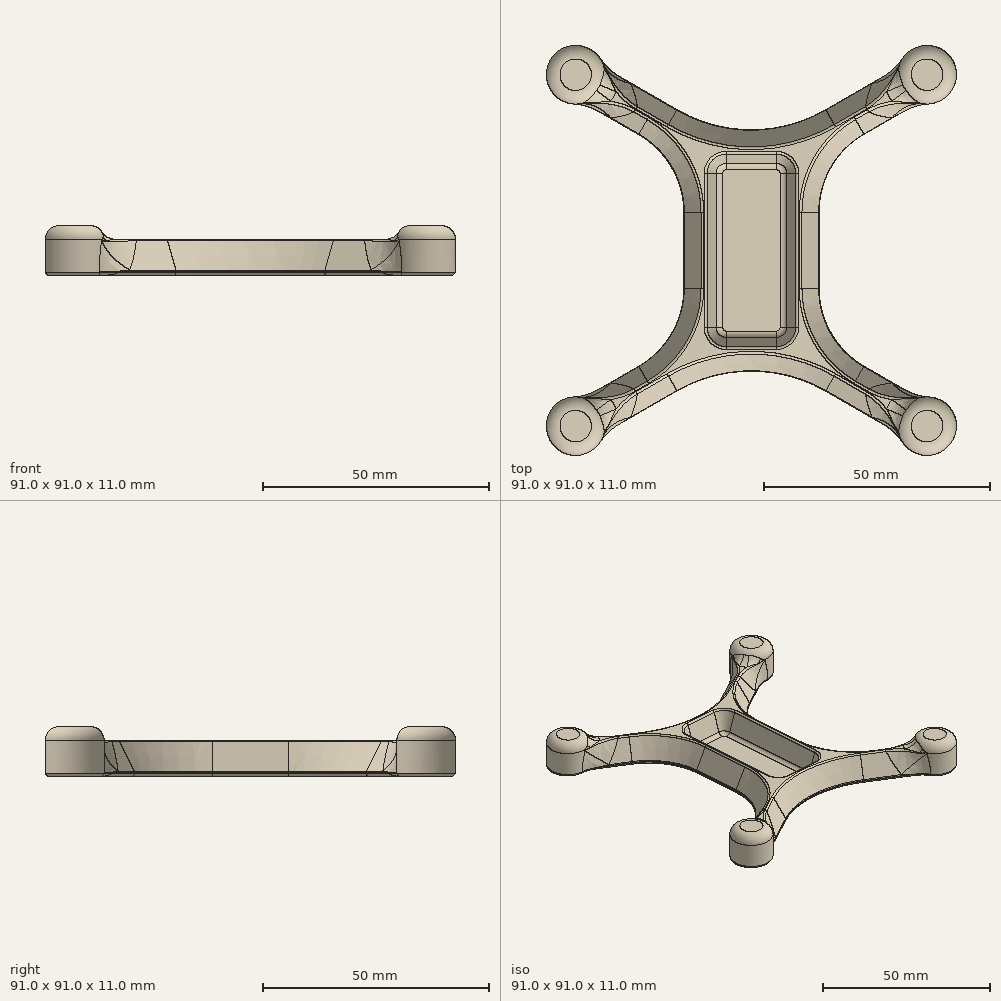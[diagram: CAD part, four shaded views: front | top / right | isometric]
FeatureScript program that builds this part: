
annotation { "Feature Type Name" : "Feature", "Feature Type Description" : "" }
export const myFeature = defineFeature(function(context is Context, id is Id, definition is map)
    precondition{}
    {
        {
            var Q0;
            Q0=qCreatedBy(makeId("Top.planeOp"),FACE);
            var sketch = newSketch(context, id + "F0", { "sketchPlane" : qUnion([Q0])});
            skLineSegment(sketch, "E0", {"start": v(-32.69, 40.55) * mm, "end": v(0, 21.68) * mm});
            skLineSegment(sketch, "E1", {"start": v(0, 21.68) * mm, "end": v(32.69, 40.55) * mm});
            skLineSegment(sketch, "E2", {"start": v(-32.69, -40.55) * mm, "end": v(0, -21.68) * mm});
            skLineSegment(sketch, "E3", {"start": v(0, -21.68) * mm, "end": v(32.69, -40.55) * mm});
            skLineSegment(sketch, "E4", {"start": v(-37.19, 32.76) * mm, "end": v(-15, 19.95) * mm});
            skLineSegment(sketch, "E5", {"start": v(-15, 19.95) * mm, "end": v(-15, -19.95) * mm});
            skLineSegment(sketch, "E6", {"start": v(-15, -19.95) * mm, "end": v(-37.19, -32.76) * mm});
            skLineSegment(sketch, "E7", {"start": v(37.19, -32.76) * mm, "end": v(15, -19.95) * mm});
            skLineSegment(sketch, "E8", {"start": v(15, -19.95) * mm, "end": v(15, 19.95) * mm});
            skLineSegment(sketch, "E9", {"start": v(15, 19.95) * mm, "end": v(37.19, 32.76) * mm});
            skArc(sketch, "E10", {"start": v(-37.19, 32.76) * mm, "mid": v(-44.63, 42.25) * mm, "end": v(-32.69, 40.55) * mm});
            skArc(sketch, "E11", {"start": v(37.19, 32.76) * mm, "mid": v(44.63, 42.25) * mm, "end": v(32.69, 40.55) * mm});
            skArc(sketch, "E12", {"start": v(37.19, -32.76) * mm, "mid": v(44.63, -42.25) * mm, "end": v(32.69, -40.55) * mm});
            skArc(sketch, "E13", {"start": v(-37.19, -32.76) * mm, "mid": v(-44.63, -42.25) * mm, "end": v(-32.69, -40.55) * mm});
            skArc(sketch, "E14", {"start": v(-34.08, 38.37) * mm, "mid": v(-33.8, 36) * mm, "end": v(-36, 35.05) * mm});
            skArc(sketch, "E15", {"start": v(34.08, 38.37) * mm, "mid": v(33.8, 36) * mm, "end": v(36, 35.05) * mm});
            skArc(sketch, "E16", {"start": v(-36, -35.05) * mm, "mid": v(-33.8, -36) * mm, "end": v(-34.08, -38.37) * mm});
            skArc(sketch, "E17", {"start": v(36, -35.05) * mm, "mid": v(33.8, -36) * mm, "end": v(34.08, -38.37) * mm});
            skArc(sketch, "E18", {"start": v(37.64, -34.97) * mm, "mid": v(42.68, -41.12) * mm, "end": v(34.83, -39.83) * mm});
            skArc(sketch, "E19", {"start": v(-37.64, -34.97) * mm, "mid": v(-42.68, -41.12) * mm, "end": v(-34.83, -39.83) * mm});
            skArc(sketch, "E20", {"start": v(-34.83, 39.83) * mm, "mid": v(-42.68, 41.13) * mm, "end": v(-37.64, 34.97) * mm});
            skArc(sketch, "E21", {"start": v(37.64, 34.97) * mm, "mid": v(42.68, 41.13) * mm, "end": v(34.83, 39.83) * mm});
            skPoint(sketch, "E22.visualSharp", {"position": v(-34.75, 38.84) * mm});
            skArc(sketch, "E22.filletArc", {"start": v(-34.83, 39.83) * mm, "mid": v(-34.56, 39.05) * mm, "end": v(-34.08, 38.37) * mm});
            skPoint(sketch, "E23.visualSharp", {"position": v(-36.74, 35.4) * mm});
            skArc(sketch, "E23.filletArc", {"start": v(-36, 35.05) * mm, "mid": v(-36.82, 35.13) * mm, "end": v(-37.64, 34.97) * mm});
            skPoint(sketch, "E24.visualSharp", {"position": v(34.75, 38.84) * mm});
            skArc(sketch, "E24.filletArc", {"start": v(34.08, 38.37) * mm, "mid": v(34.56, 39.05) * mm, "end": v(34.83, 39.83) * mm});
            skPoint(sketch, "E25.visualSharp", {"position": v(36.74, 35.4) * mm});
            skArc(sketch, "E25.filletArc", {"start": v(37.64, 34.97) * mm, "mid": v(36.82, 35.13) * mm, "end": v(36, 35.05) * mm});
            skPoint(sketch, "E26.visualSharp", {"position": v(36.74, -35.4) * mm});
            skArc(sketch, "E26.filletArc", {"start": v(36, -35.05) * mm, "mid": v(36.82, -35.13) * mm, "end": v(37.64, -34.97) * mm});
            skPoint(sketch, "E27.visualSharp", {"position": v(34.75, -38.84) * mm});
            skArc(sketch, "E27.filletArc", {"start": v(34.83, -39.83) * mm, "mid": v(34.56, -39.05) * mm, "end": v(34.08, -38.37) * mm});
            skPoint(sketch, "E28.visualSharp", {"position": v(-36.74, -35.4) * mm});
            skArc(sketch, "E28.filletArc", {"start": v(-37.64, -34.97) * mm, "mid": v(-36.82, -35.13) * mm, "end": v(-36, -35.05) * mm});
            skPoint(sketch, "E29.visualSharp", {"position": v(-34.75, -38.84) * mm});
            skArc(sketch, "E29.filletArc", {"start": v(-34.08, -38.37) * mm, "mid": v(-34.56, -39.05) * mm, "end": v(-34.83, -39.83) * mm});
            skSolve(sketch);
        }
        {
            var Q0;
            Q0 = qSketchRegion(id + "F0", true);
            extrude(context, id + "F1", {"entities" : qUnion([Q0]), "depth" : 8 * mm, "offsetDistance" : 25 * mm});
        }
        {
            var Q0;
            Q0=qCreatedBy(makeId("Front.planeOp"),FACE);
            var sketch = newSketch(context, id + "F2", { "sketchPlane" : qUnion([Q0])});
            skLineSegment(sketch, "E30.bottom", {"start": v(-7.5, 10.6) * mm, "end": v(7.5, 10.6) * mm});
            skLineSegment(sketch, "E30.top", {"start": v(-7.5, 0.6) * mm, "end": v(7.5, 0.6) * mm});
            skLineSegment(sketch, "E30.left", {"start": v(-7.5, 10.6) * mm, "end": v(-7.5, 0.6) * mm});
            skLineSegment(sketch, "E30.right", {"start": v(7.5, 10.6) * mm, "end": v(7.5, 0.6) * mm});
            skSolve(sketch);
        }
        {
            var Q0;
            Q0 = qSketchRegion(id + "F2", true);
            extrude(context, id + "F3", {"entities" : qUnion([Q0]), "operationType" : NewBodyOperationType.REMOVE, "oppositeDirection" : true, "depth" : 19 * mm, "offsetDistance" : 25 * mm, "hasSecondDirection" : true, "secondDirectionOppositeDirection" : false, "secondDirectionDepth" : 19 * mm});
        }
        {
            var Q0;
            Q0=makeQuery(id+"F1.opExtrude","CAP_FACE",FACE,{"disambiguationData":[OSD([sQuery(id+"F0.wireOp",EDGE,"E0"),sQuery(id+"F0.wireOp",EDGE,"E1"),sQuery(id+"F0.wireOp",EDGE,"E2"),sQuery(id+"F0.wireOp",EDGE,"E3"),sQuery(id+"F0.wireOp",EDGE,"E4"),sQuery(id+"F0.wireOp",EDGE,"E5"),sQuery(id+"F0.wireOp",EDGE,"E6"),sQuery(id+"F0.wireOp",EDGE,"E7"),sQuery(id+"F0.wireOp",EDGE,"E8"),sQuery(id+"F0.wireOp",EDGE,"E9"),sQuery(id+"F0.wireOp",EDGE,"E10"),sQuery(id+"F0.wireOp",EDGE,"E11"),sQuery(id+"F0.wireOp",EDGE,"E12"),sQuery(id+"F0.wireOp",EDGE,"E13"),sQuery(id+"F0.wireOp",EDGE,"E14"),sQuery(id+"F0.wireOp",EDGE,"E15"),sQuery(id+"F0.wireOp",EDGE,"E16"),sQuery(id+"F0.wireOp",EDGE,"E17"),sQuery(id+"F0.wireOp",EDGE,"E18"),sQuery(id+"F0.wireOp",EDGE,"E19"),sQuery(id+"F0.wireOp",EDGE,"E20"),sQuery(id+"F0.wireOp",EDGE,"E21")])],"isStart":false});
            var sketch = newSketch(context, id + "F4", { "sketchPlane" : qUnion([Q0])});
            skCircle(sketch, "E31", {"center": v(-39, 39) * mm, "radius": 6.5 * mm});
            skCircle(sketch, "E32", {"center": v(39, 39) * mm, "radius": 6.5 * mm});
            skCircle(sketch, "E33", {"center": v(39, -39) * mm, "radius": 6.5 * mm});
            skCircle(sketch, "E34", {"center": v(-39, -39) * mm, "radius": 6.5 * mm});
            skSolve(sketch);
        }
        {
            var Q0;
            Q0 = qSketchRegion(id + "F4", true);
            extrude(context, id + "F5", {"entities" : qUnion([Q0]), "operationType" : NewBodyOperationType.ADD, "depth" : 3 * mm, "offsetDistance" : 25 * mm});
        }
        {
            var Q0;
            Q0=makeQuery(id+"F1.opExtrude","SWEPT_EDGE",EDGE,{"disambiguationData":[OSD([sQuery(id+"F0.wireOp",EDGE,"E0"),sQuery(id+"F0.wireOp",EDGE,"E1")])]});
            var Q1;
            Q1=makeQuery(id+"F1.opExtrude","SWEPT_EDGE",EDGE,{"disambiguationData":[OSD([sQuery(id+"F0.wireOp",EDGE,"E2"),sQuery(id+"F0.wireOp",EDGE,"E3")])]});
            fillet(context, id + "F6", {"entities" : qUnion([Q0, Q1]), "radius" : 33 * mm, "tangentPropagation" : true, "allowEdgeOverflow" : false});
        }
        {
            var Q0;
            Q0=makeQuery(id+"F1.opExtrude","SWEPT_EDGE",EDGE,{"disambiguationData":[OSD([sQuery(id+"F0.wireOp",EDGE,"E4"),sQuery(id+"F0.wireOp",EDGE,"E5")])]});
            var Q1;
            Q1=makeQuery(id+"F1.opExtrude","SWEPT_EDGE",EDGE,{"disambiguationData":[OSD([sQuery(id+"F0.wireOp",EDGE,"E5"),sQuery(id+"F0.wireOp",EDGE,"E6")])]});
            var Q2;
            Q2=makeQuery(id+"F1.opExtrude","SWEPT_EDGE",EDGE,{"disambiguationData":[OSD([sQuery(id+"F0.wireOp",EDGE,"E8"),sQuery(id+"F0.wireOp",EDGE,"E9")])]});
            var Q3;
            Q3=makeQuery(id+"F1.opExtrude","SWEPT_EDGE",EDGE,{"disambiguationData":[OSD([sQuery(id+"F0.wireOp",EDGE,"E7"),sQuery(id+"F0.wireOp",EDGE,"E8")])]});
            fillet(context, id + "F7", {"entities" : qUnion([Q0, Q1, Q2, Q3]), "radius" : 20 * mm, "tangentPropagation" : true, "allowEdgeOverflow" : false});
        }
        {
            var Q0;
            Q0=makeQuery(id+"F1.opExtrude","CAP_EDGE",EDGE,{"disambiguationData":[OSD([sQuery(id+"F0.wireOp",EDGE,"E2")])],"isStart":false});
            var Q1;
            Q1=makeQuery(id+"F1.opExtrude","CAP_EDGE",EDGE,{"disambiguationData":[OSD([sQuery(id+"F0.wireOp",EDGE,"E6")])],"isStart":false});
            var Q2;
            Q2=makeQuery(id+"F1.opExtrude","CAP_EDGE",EDGE,{"disambiguationData":[OSD([sQuery(id+"F0.wireOp",EDGE,"E3")])],"isStart":false});
            var Q3;
            Q3=makeQuery(id+"F1.opExtrude","CAP_EDGE",EDGE,{"disambiguationData":[OSD([sQuery(id+"F0.wireOp",EDGE,"E7")])],"isStart":false});
            var Q4;
            Q4=makeQuery(id+"F1.opExtrude","CAP_EDGE",EDGE,{"disambiguationData":[OSD([sQuery(id+"F0.wireOp",EDGE,"E1")])],"isStart":false});
            var Q5;
            Q5=makeQuery(id+"F1.opExtrude","CAP_EDGE",EDGE,{"disambiguationData":[OSD([sQuery(id+"F0.wireOp",EDGE,"E0")])],"isStart":false});
            var Q6;
            Q6=makeQuery(id+"F1.opExtrude","CAP_EDGE",EDGE,{"disambiguationData":[OSD([sQuery(id+"F0.wireOp",EDGE,"E4")])],"isStart":false});
            var Q7;
            Q7=makeQuery(id+"F1.opExtrude","CAP_EDGE",EDGE,{"disambiguationData":[OSD([sQuery(id+"F0.wireOp",EDGE,"E9")])],"isStart":false});
            chamfer(context, id + "F8", {"entities" : qUnion([Q0, Q1, Q2, Q3, Q4, Q5, Q6, Q7]), "chamferType" : ChamferType.TWO_OFFSETS, "width1" : 4 * mm, "oppositeDirection" : false, "width2" : 7 * mm, "tangentPropagation" : true});
        }
        {
            var Q0;
            Q0=makeQuery(id+"F3.boolean.opBoolean","COPY",EDGE,{"derivedFrom":makeQuery(id+"F3.opExtrude","CAP_EDGE",EDGE,{"disambiguationData":[OSD([sQuery(id+"F2.wireOp",EDGE,"E30.left")])],"isStart":false})});
            var Q1;
            Q1=makeQuery(id+"F3.boolean.opBoolean","COPY",EDGE,{"derivedFrom":makeQuery(id+"F3.opExtrude","CAP_EDGE",EDGE,{"disambiguationData":[OSD([sQuery(id+"F2.wireOp",EDGE,"E30.right")])],"isStart":false})});
            var Q2;
            Q2=makeQuery(id+"F3.boolean.opBoolean","COPY",EDGE,{"derivedFrom":makeQuery(id+"F3.opExtrude","CAP_EDGE",EDGE,{"disambiguationData":[OSD([sQuery(id+"F2.wireOp",EDGE,"E30.left")])],"isStart":true})});
            var Q3;
            Q3=makeQuery(id+"F3.boolean.opBoolean","COPY",EDGE,{"derivedFrom":makeQuery(id+"F3.opExtrude","CAP_EDGE",EDGE,{"disambiguationData":[OSD([sQuery(id+"F2.wireOp",EDGE,"E30.right")])],"isStart":true})});
            fillet(context, id + "F9", {"entities" : qUnion([Q0, Q1, Q2, Q3]), "radius" : 2 * mm, "tangentPropagation" : true, "allowEdgeOverflow" : false});
        }
        {
            var Q0;
            Q0=makeQuery(id+"F3.boolean.opBoolean","INTERSECT",EDGE,{"derivedFrom":[makeQuery(id+"F1.opExtrude","CAP_FACE",FACE,{"disambiguationData":[OSD([sQuery(id+"F0.wireOp",EDGE,"E0"),sQuery(id+"F0.wireOp",EDGE,"E1"),sQuery(id+"F0.wireOp",EDGE,"E2"),sQuery(id+"F0.wireOp",EDGE,"E3"),sQuery(id+"F0.wireOp",EDGE,"E4"),sQuery(id+"F0.wireOp",EDGE,"E5"),sQuery(id+"F0.wireOp",EDGE,"E6"),sQuery(id+"F0.wireOp",EDGE,"E7"),sQuery(id+"F0.wireOp",EDGE,"E8"),sQuery(id+"F0.wireOp",EDGE,"E9"),sQuery(id+"F0.wireOp",EDGE,"E10"),sQuery(id+"F0.wireOp",EDGE,"E11"),sQuery(id+"F0.wireOp",EDGE,"E12"),sQuery(id+"F0.wireOp",EDGE,"E13"),sQuery(id+"F0.wireOp",EDGE,"E14"),sQuery(id+"F0.wireOp",EDGE,"E15"),sQuery(id+"F0.wireOp",EDGE,"E16"),sQuery(id+"F0.wireOp",EDGE,"E17"),sQuery(id+"F0.wireOp",EDGE,"E18"),sQuery(id+"F0.wireOp",EDGE,"E19"),sQuery(id+"F0.wireOp",EDGE,"E20"),sQuery(id+"F0.wireOp",EDGE,"E21"),sQuery(id+"F0.wireOp",EDGE,"E22.filletArc"),sQuery(id+"F0.wireOp",EDGE,"E23.filletArc"),sQuery(id+"F0.wireOp",EDGE,"E24.filletArc"),sQuery(id+"F0.wireOp",EDGE,"E25.filletArc"),sQuery(id+"F0.wireOp",EDGE,"E26.filletArc"),sQuery(id+"F0.wireOp",EDGE,"E27.filletArc"),sQuery(id+"F0.wireOp",EDGE,"E28.filletArc"),sQuery(id+"F0.wireOp",EDGE,"E29.filletArc")])],"isStart":false}),makeQuery(id+"F3.opExtrude","CAP_FACE",FACE,{"disambiguationData":[OSD([sQuery(id+"F2.wireOp",EDGE,"E30.bottom"),sQuery(id+"F2.wireOp",EDGE,"E30.top"),sQuery(id+"F2.wireOp",EDGE,"E30.left"),sQuery(id+"F2.wireOp",EDGE,"E30.right")])],"isStart":false})]});
            chamfer(context, id + "F10", {"entities" : qUnion([Q0]), "chamferType" : ChamferType.TWO_OFFSETS, "width1" : 2.5 * mm, "oppositeDirection" : false, "width2" : 7.4 * mm, "tangentPropagation" : true});
        }
        {
            var Q0;
            Q0=makeQuery(id+"F5.opExtrude","CAP_FACE",FACE,{"disambiguationData":[OSD([sQuery(id+"F4.wireOp",EDGE,"E34")])],"isStart":true});
            var Q1;
            Q1=makeQuery(id+"F5.opExtrude","CAP_FACE",FACE,{"disambiguationData":[OSD([sQuery(id+"F4.wireOp",EDGE,"E33")])],"isStart":true});
            var Q2;
            Q2=makeQuery(id+"F5.opExtrude","CAP_FACE",FACE,{"disambiguationData":[OSD([sQuery(id+"F4.wireOp",EDGE,"E32")])],"isStart":true});
            var Q3;
            Q3=makeQuery(id+"F5.opExtrude","CAP_FACE",FACE,{"disambiguationData":[OSD([sQuery(id+"F4.wireOp",EDGE,"E31")])],"isStart":true});
            fillet(context, id + "F11", {"entities" : qUnion([Q0, Q1, Q2, Q3]), "radius" : 2 * mm, "tangentPropagation" : true, "allowEdgeOverflow" : false});
        }
        {
            var Q0;
            Q0=makeQuery(id+"F1.opExtrude","CAP_FACE",FACE,{"disambiguationData":[OSD([sQuery(id+"F0.wireOp",EDGE,"E0"),sQuery(id+"F0.wireOp",EDGE,"E1"),sQuery(id+"F0.wireOp",EDGE,"E2"),sQuery(id+"F0.wireOp",EDGE,"E3"),sQuery(id+"F0.wireOp",EDGE,"E4"),sQuery(id+"F0.wireOp",EDGE,"E5"),sQuery(id+"F0.wireOp",EDGE,"E6"),sQuery(id+"F0.wireOp",EDGE,"E7"),sQuery(id+"F0.wireOp",EDGE,"E8"),sQuery(id+"F0.wireOp",EDGE,"E9"),sQuery(id+"F0.wireOp",EDGE,"E10"),sQuery(id+"F0.wireOp",EDGE,"E11"),sQuery(id+"F0.wireOp",EDGE,"E12"),sQuery(id+"F0.wireOp",EDGE,"E13"),sQuery(id+"F0.wireOp",EDGE,"E14"),sQuery(id+"F0.wireOp",EDGE,"E15"),sQuery(id+"F0.wireOp",EDGE,"E16"),sQuery(id+"F0.wireOp",EDGE,"E17"),sQuery(id+"F0.wireOp",EDGE,"E18"),sQuery(id+"F0.wireOp",EDGE,"E19"),sQuery(id+"F0.wireOp",EDGE,"E20"),sQuery(id+"F0.wireOp",EDGE,"E21"),sQuery(id+"F0.wireOp",EDGE,"E22.filletArc"),sQuery(id+"F0.wireOp",EDGE,"E23.filletArc"),sQuery(id+"F0.wireOp",EDGE,"E24.filletArc"),sQuery(id+"F0.wireOp",EDGE,"E25.filletArc"),sQuery(id+"F0.wireOp",EDGE,"E26.filletArc"),sQuery(id+"F0.wireOp",EDGE,"E27.filletArc"),sQuery(id+"F0.wireOp",EDGE,"E28.filletArc"),sQuery(id+"F0.wireOp",EDGE,"E29.filletArc")])],"isStart":true});
            var Q1;
            {var subQ0=sQuery(id+"F0.wireOp",EDGE,"E3");var subQ1=sQuery(id+"F0.wireOp",EDGE,"E2");Q1=makeQuery(id+"F8.opChamfer","BLEND_EDGE",EDGE,{"blendedFrom":[makeQuery(id+"F6.opFillet","BLEND_EDGE",EDGE,{"blendedFrom":[makeQuery(id+"F1.opExtrude","SWEPT_EDGE",EDGE,{"disambiguationData":[OSD([subQ1,subQ0])]}),makeQuery(id+"F1.opExtrude","CAP_FACE",FACE,{"disambiguationData":[OSD([sQuery(id+"F0.wireOp",EDGE,"E0"),sQuery(id+"F0.wireOp",EDGE,"E1"),subQ1,subQ0,sQuery(id+"F0.wireOp",EDGE,"E4"),sQuery(id+"F0.wireOp",EDGE,"E5"),sQuery(id+"F0.wireOp",EDGE,"E6"),sQuery(id+"F0.wireOp",EDGE,"E7"),sQuery(id+"F0.wireOp",EDGE,"E8"),sQuery(id+"F0.wireOp",EDGE,"E9"),sQuery(id+"F0.wireOp",EDGE,"E10"),sQuery(id+"F0.wireOp",EDGE,"E11"),sQuery(id+"F0.wireOp",EDGE,"E12"),sQuery(id+"F0.wireOp",EDGE,"E13"),sQuery(id+"F0.wireOp",EDGE,"E14"),sQuery(id+"F0.wireOp",EDGE,"E15"),sQuery(id+"F0.wireOp",EDGE,"E16"),sQuery(id+"F0.wireOp",EDGE,"E17"),sQuery(id+"F0.wireOp",EDGE,"E18"),sQuery(id+"F0.wireOp",EDGE,"E19"),sQuery(id+"F0.wireOp",EDGE,"E20"),sQuery(id+"F0.wireOp",EDGE,"E21"),sQuery(id+"F0.wireOp",EDGE,"E22.filletArc"),sQuery(id+"F0.wireOp",EDGE,"E23.filletArc"),sQuery(id+"F0.wireOp",EDGE,"E24.filletArc"),sQuery(id+"F0.wireOp",EDGE,"E25.filletArc"),sQuery(id+"F0.wireOp",EDGE,"E26.filletArc"),sQuery(id+"F0.wireOp",EDGE,"E27.filletArc"),sQuery(id+"F0.wireOp",EDGE,"E28.filletArc"),sQuery(id+"F0.wireOp",EDGE,"E29.filletArc")])],"isStart":false})],"blendedInto":[makeQuery(id+"F1.opExtrude","CAP_FACE",FACE,{"disambiguationData":[OSD([sQuery(id+"F0.wireOp",EDGE,"E0"),sQuery(id+"F0.wireOp",EDGE,"E1"),subQ1,subQ0,sQuery(id+"F0.wireOp",EDGE,"E4"),sQuery(id+"F0.wireOp",EDGE,"E5"),sQuery(id+"F0.wireOp",EDGE,"E6"),sQuery(id+"F0.wireOp",EDGE,"E7"),sQuery(id+"F0.wireOp",EDGE,"E8"),sQuery(id+"F0.wireOp",EDGE,"E9"),sQuery(id+"F0.wireOp",EDGE,"E10"),sQuery(id+"F0.wireOp",EDGE,"E11"),sQuery(id+"F0.wireOp",EDGE,"E12"),sQuery(id+"F0.wireOp",EDGE,"E13"),sQuery(id+"F0.wireOp",EDGE,"E14"),sQuery(id+"F0.wireOp",EDGE,"E15"),sQuery(id+"F0.wireOp",EDGE,"E16"),sQuery(id+"F0.wireOp",EDGE,"E17"),sQuery(id+"F0.wireOp",EDGE,"E18"),sQuery(id+"F0.wireOp",EDGE,"E19"),sQuery(id+"F0.wireOp",EDGE,"E20"),sQuery(id+"F0.wireOp",EDGE,"E21"),sQuery(id+"F0.wireOp",EDGE,"E22.filletArc"),sQuery(id+"F0.wireOp",EDGE,"E23.filletArc"),sQuery(id+"F0.wireOp",EDGE,"E24.filletArc"),sQuery(id+"F0.wireOp",EDGE,"E25.filletArc"),sQuery(id+"F0.wireOp",EDGE,"E26.filletArc"),sQuery(id+"F0.wireOp",EDGE,"E27.filletArc"),sQuery(id+"F0.wireOp",EDGE,"E28.filletArc"),sQuery(id+"F0.wireOp",EDGE,"E29.filletArc")])],"isStart":false})]}),makeQuery(id+"F6.opFillet","BLEND_FACE",FACE,{"disambiguationData":[OSD([subQ1,subQ0])]})],"blendedInto":[makeQuery(id+"F6.opFillet","BLEND_FACE",FACE,{"disambiguationData":[OSD([subQ1,subQ0])]})]});}
            var Q2;
            {var subQ0=sQuery(id+"F0.wireOp",EDGE,"E5");var subQ1=sQuery(id+"F0.wireOp",EDGE,"E4");Q2=makeQuery(id+"F8.opChamfer","BLEND_EDGE",EDGE,{"blendedFrom":[makeQuery(id+"F7.opFillet","BLEND_EDGE",EDGE,{"blendedFrom":[makeQuery(id+"F1.opExtrude","SWEPT_EDGE",EDGE,{"disambiguationData":[OSD([subQ1,subQ0])]}),makeQuery(id+"F1.opExtrude","CAP_FACE",FACE,{"disambiguationData":[OSD([sQuery(id+"F0.wireOp",EDGE,"E0"),sQuery(id+"F0.wireOp",EDGE,"E1"),sQuery(id+"F0.wireOp",EDGE,"E2"),sQuery(id+"F0.wireOp",EDGE,"E3"),subQ1,subQ0,sQuery(id+"F0.wireOp",EDGE,"E6"),sQuery(id+"F0.wireOp",EDGE,"E7"),sQuery(id+"F0.wireOp",EDGE,"E8"),sQuery(id+"F0.wireOp",EDGE,"E9"),sQuery(id+"F0.wireOp",EDGE,"E10"),sQuery(id+"F0.wireOp",EDGE,"E11"),sQuery(id+"F0.wireOp",EDGE,"E12"),sQuery(id+"F0.wireOp",EDGE,"E13"),sQuery(id+"F0.wireOp",EDGE,"E14"),sQuery(id+"F0.wireOp",EDGE,"E15"),sQuery(id+"F0.wireOp",EDGE,"E16"),sQuery(id+"F0.wireOp",EDGE,"E17"),sQuery(id+"F0.wireOp",EDGE,"E18"),sQuery(id+"F0.wireOp",EDGE,"E19"),sQuery(id+"F0.wireOp",EDGE,"E20"),sQuery(id+"F0.wireOp",EDGE,"E21"),sQuery(id+"F0.wireOp",EDGE,"E22.filletArc"),sQuery(id+"F0.wireOp",EDGE,"E23.filletArc"),sQuery(id+"F0.wireOp",EDGE,"E24.filletArc"),sQuery(id+"F0.wireOp",EDGE,"E25.filletArc"),sQuery(id+"F0.wireOp",EDGE,"E26.filletArc"),sQuery(id+"F0.wireOp",EDGE,"E27.filletArc"),sQuery(id+"F0.wireOp",EDGE,"E28.filletArc"),sQuery(id+"F0.wireOp",EDGE,"E29.filletArc")])],"isStart":false})],"blendedInto":[makeQuery(id+"F1.opExtrude","CAP_FACE",FACE,{"disambiguationData":[OSD([sQuery(id+"F0.wireOp",EDGE,"E0"),sQuery(id+"F0.wireOp",EDGE,"E1"),sQuery(id+"F0.wireOp",EDGE,"E2"),sQuery(id+"F0.wireOp",EDGE,"E3"),subQ1,subQ0,sQuery(id+"F0.wireOp",EDGE,"E6"),sQuery(id+"F0.wireOp",EDGE,"E7"),sQuery(id+"F0.wireOp",EDGE,"E8"),sQuery(id+"F0.wireOp",EDGE,"E9"),sQuery(id+"F0.wireOp",EDGE,"E10"),sQuery(id+"F0.wireOp",EDGE,"E11"),sQuery(id+"F0.wireOp",EDGE,"E12"),sQuery(id+"F0.wireOp",EDGE,"E13"),sQuery(id+"F0.wireOp",EDGE,"E14"),sQuery(id+"F0.wireOp",EDGE,"E15"),sQuery(id+"F0.wireOp",EDGE,"E16"),sQuery(id+"F0.wireOp",EDGE,"E17"),sQuery(id+"F0.wireOp",EDGE,"E18"),sQuery(id+"F0.wireOp",EDGE,"E19"),sQuery(id+"F0.wireOp",EDGE,"E20"),sQuery(id+"F0.wireOp",EDGE,"E21"),sQuery(id+"F0.wireOp",EDGE,"E22.filletArc"),sQuery(id+"F0.wireOp",EDGE,"E23.filletArc"),sQuery(id+"F0.wireOp",EDGE,"E24.filletArc"),sQuery(id+"F0.wireOp",EDGE,"E25.filletArc"),sQuery(id+"F0.wireOp",EDGE,"E26.filletArc"),sQuery(id+"F0.wireOp",EDGE,"E27.filletArc"),sQuery(id+"F0.wireOp",EDGE,"E28.filletArc"),sQuery(id+"F0.wireOp",EDGE,"E29.filletArc")])],"isStart":false})]}),makeQuery(id+"F7.opFillet","BLEND_FACE",FACE,{"disambiguationData":[OSD([subQ1,subQ0])]})],"blendedInto":[makeQuery(id+"F7.opFillet","BLEND_FACE",FACE,{"disambiguationData":[OSD([subQ1,subQ0])]})]});}
            var Q3;
            {var subQ0=sQuery(id+"F0.wireOp",EDGE,"E9");var subQ1=sQuery(id+"F0.wireOp",EDGE,"E8");Q3=makeQuery(id+"F8.opChamfer","BLEND_EDGE",EDGE,{"blendedFrom":[makeQuery(id+"F7.opFillet","BLEND_EDGE",EDGE,{"blendedFrom":[makeQuery(id+"F1.opExtrude","SWEPT_EDGE",EDGE,{"disambiguationData":[OSD([subQ1,subQ0])]}),makeQuery(id+"F1.opExtrude","CAP_FACE",FACE,{"disambiguationData":[OSD([sQuery(id+"F0.wireOp",EDGE,"E0"),sQuery(id+"F0.wireOp",EDGE,"E1"),sQuery(id+"F0.wireOp",EDGE,"E2"),sQuery(id+"F0.wireOp",EDGE,"E3"),sQuery(id+"F0.wireOp",EDGE,"E4"),sQuery(id+"F0.wireOp",EDGE,"E5"),sQuery(id+"F0.wireOp",EDGE,"E6"),sQuery(id+"F0.wireOp",EDGE,"E7"),subQ1,subQ0,sQuery(id+"F0.wireOp",EDGE,"E10"),sQuery(id+"F0.wireOp",EDGE,"E11"),sQuery(id+"F0.wireOp",EDGE,"E12"),sQuery(id+"F0.wireOp",EDGE,"E13"),sQuery(id+"F0.wireOp",EDGE,"E14"),sQuery(id+"F0.wireOp",EDGE,"E15"),sQuery(id+"F0.wireOp",EDGE,"E16"),sQuery(id+"F0.wireOp",EDGE,"E17"),sQuery(id+"F0.wireOp",EDGE,"E18"),sQuery(id+"F0.wireOp",EDGE,"E19"),sQuery(id+"F0.wireOp",EDGE,"E20"),sQuery(id+"F0.wireOp",EDGE,"E21"),sQuery(id+"F0.wireOp",EDGE,"E22.filletArc"),sQuery(id+"F0.wireOp",EDGE,"E23.filletArc"),sQuery(id+"F0.wireOp",EDGE,"E24.filletArc"),sQuery(id+"F0.wireOp",EDGE,"E25.filletArc"),sQuery(id+"F0.wireOp",EDGE,"E26.filletArc"),sQuery(id+"F0.wireOp",EDGE,"E27.filletArc"),sQuery(id+"F0.wireOp",EDGE,"E28.filletArc"),sQuery(id+"F0.wireOp",EDGE,"E29.filletArc")])],"isStart":false})],"blendedInto":[makeQuery(id+"F1.opExtrude","CAP_FACE",FACE,{"disambiguationData":[OSD([sQuery(id+"F0.wireOp",EDGE,"E0"),sQuery(id+"F0.wireOp",EDGE,"E1"),sQuery(id+"F0.wireOp",EDGE,"E2"),sQuery(id+"F0.wireOp",EDGE,"E3"),sQuery(id+"F0.wireOp",EDGE,"E4"),sQuery(id+"F0.wireOp",EDGE,"E5"),sQuery(id+"F0.wireOp",EDGE,"E6"),sQuery(id+"F0.wireOp",EDGE,"E7"),subQ1,subQ0,sQuery(id+"F0.wireOp",EDGE,"E10"),sQuery(id+"F0.wireOp",EDGE,"E11"),sQuery(id+"F0.wireOp",EDGE,"E12"),sQuery(id+"F0.wireOp",EDGE,"E13"),sQuery(id+"F0.wireOp",EDGE,"E14"),sQuery(id+"F0.wireOp",EDGE,"E15"),sQuery(id+"F0.wireOp",EDGE,"E16"),sQuery(id+"F0.wireOp",EDGE,"E17"),sQuery(id+"F0.wireOp",EDGE,"E18"),sQuery(id+"F0.wireOp",EDGE,"E19"),sQuery(id+"F0.wireOp",EDGE,"E20"),sQuery(id+"F0.wireOp",EDGE,"E21"),sQuery(id+"F0.wireOp",EDGE,"E22.filletArc"),sQuery(id+"F0.wireOp",EDGE,"E23.filletArc"),sQuery(id+"F0.wireOp",EDGE,"E24.filletArc"),sQuery(id+"F0.wireOp",EDGE,"E25.filletArc"),sQuery(id+"F0.wireOp",EDGE,"E26.filletArc"),sQuery(id+"F0.wireOp",EDGE,"E27.filletArc"),sQuery(id+"F0.wireOp",EDGE,"E28.filletArc"),sQuery(id+"F0.wireOp",EDGE,"E29.filletArc")])],"isStart":false})]}),makeQuery(id+"F7.opFillet","BLEND_FACE",FACE,{"disambiguationData":[OSD([subQ1,subQ0])]})],"blendedInto":[makeQuery(id+"F7.opFillet","BLEND_FACE",FACE,{"disambiguationData":[OSD([subQ1,subQ0])]})]});}
            var Q4;
            {var subQ0=sQuery(id+"F0.wireOp",EDGE,"E1");var subQ1=sQuery(id+"F0.wireOp",EDGE,"E0");Q4=makeQuery(id+"F8.opChamfer","BLEND_EDGE",EDGE,{"blendedFrom":[makeQuery(id+"F6.opFillet","BLEND_EDGE",EDGE,{"blendedFrom":[makeQuery(id+"F1.opExtrude","SWEPT_EDGE",EDGE,{"disambiguationData":[OSD([subQ1,subQ0])]}),makeQuery(id+"F1.opExtrude","CAP_FACE",FACE,{"disambiguationData":[OSD([subQ1,subQ0,sQuery(id+"F0.wireOp",EDGE,"E2"),sQuery(id+"F0.wireOp",EDGE,"E3"),sQuery(id+"F0.wireOp",EDGE,"E4"),sQuery(id+"F0.wireOp",EDGE,"E5"),sQuery(id+"F0.wireOp",EDGE,"E6"),sQuery(id+"F0.wireOp",EDGE,"E7"),sQuery(id+"F0.wireOp",EDGE,"E8"),sQuery(id+"F0.wireOp",EDGE,"E9"),sQuery(id+"F0.wireOp",EDGE,"E10"),sQuery(id+"F0.wireOp",EDGE,"E11"),sQuery(id+"F0.wireOp",EDGE,"E12"),sQuery(id+"F0.wireOp",EDGE,"E13"),sQuery(id+"F0.wireOp",EDGE,"E14"),sQuery(id+"F0.wireOp",EDGE,"E15"),sQuery(id+"F0.wireOp",EDGE,"E16"),sQuery(id+"F0.wireOp",EDGE,"E17"),sQuery(id+"F0.wireOp",EDGE,"E18"),sQuery(id+"F0.wireOp",EDGE,"E19"),sQuery(id+"F0.wireOp",EDGE,"E20"),sQuery(id+"F0.wireOp",EDGE,"E21"),sQuery(id+"F0.wireOp",EDGE,"E22.filletArc"),sQuery(id+"F0.wireOp",EDGE,"E23.filletArc"),sQuery(id+"F0.wireOp",EDGE,"E24.filletArc"),sQuery(id+"F0.wireOp",EDGE,"E25.filletArc"),sQuery(id+"F0.wireOp",EDGE,"E26.filletArc"),sQuery(id+"F0.wireOp",EDGE,"E27.filletArc"),sQuery(id+"F0.wireOp",EDGE,"E28.filletArc"),sQuery(id+"F0.wireOp",EDGE,"E29.filletArc")])],"isStart":false})],"blendedInto":[makeQuery(id+"F1.opExtrude","CAP_FACE",FACE,{"disambiguationData":[OSD([subQ1,subQ0,sQuery(id+"F0.wireOp",EDGE,"E2"),sQuery(id+"F0.wireOp",EDGE,"E3"),sQuery(id+"F0.wireOp",EDGE,"E4"),sQuery(id+"F0.wireOp",EDGE,"E5"),sQuery(id+"F0.wireOp",EDGE,"E6"),sQuery(id+"F0.wireOp",EDGE,"E7"),sQuery(id+"F0.wireOp",EDGE,"E8"),sQuery(id+"F0.wireOp",EDGE,"E9"),sQuery(id+"F0.wireOp",EDGE,"E10"),sQuery(id+"F0.wireOp",EDGE,"E11"),sQuery(id+"F0.wireOp",EDGE,"E12"),sQuery(id+"F0.wireOp",EDGE,"E13"),sQuery(id+"F0.wireOp",EDGE,"E14"),sQuery(id+"F0.wireOp",EDGE,"E15"),sQuery(id+"F0.wireOp",EDGE,"E16"),sQuery(id+"F0.wireOp",EDGE,"E17"),sQuery(id+"F0.wireOp",EDGE,"E18"),sQuery(id+"F0.wireOp",EDGE,"E19"),sQuery(id+"F0.wireOp",EDGE,"E20"),sQuery(id+"F0.wireOp",EDGE,"E21"),sQuery(id+"F0.wireOp",EDGE,"E22.filletArc"),sQuery(id+"F0.wireOp",EDGE,"E23.filletArc"),sQuery(id+"F0.wireOp",EDGE,"E24.filletArc"),sQuery(id+"F0.wireOp",EDGE,"E25.filletArc"),sQuery(id+"F0.wireOp",EDGE,"E26.filletArc"),sQuery(id+"F0.wireOp",EDGE,"E27.filletArc"),sQuery(id+"F0.wireOp",EDGE,"E28.filletArc"),sQuery(id+"F0.wireOp",EDGE,"E29.filletArc")])],"isStart":false})]}),makeQuery(id+"F6.opFillet","BLEND_FACE",FACE,{"disambiguationData":[OSD([subQ1,subQ0])]})],"blendedInto":[makeQuery(id+"F6.opFillet","BLEND_FACE",FACE,{"disambiguationData":[OSD([subQ1,subQ0])]})]});}
            fillet(context, id + "F12", {"entities" : qUnion([Q0, Q1, Q2, Q3, Q4]), "radius" : .7 * mm, "tangentPropagation" : true, "allowEdgeOverflow" : false});
        }
        {
            var Q0;
            Q0=makeQuery(id+"F8.opChamfer","BLEND_EDGE",EDGE,{"blendedFrom":[makeQuery(id+"F1.opExtrude","CAP_EDGE",EDGE,{"disambiguationData":[OSD([sQuery(id+"F0.wireOp",EDGE,"E2")])],"isStart":false}),makeQuery(id+"F5.boolean.opBoolean","MERGE",FACE,{"derivedFrom":[makeQuery(id+"F1.opExtrude","SWEPT_FACE",FACE,{"disambiguationData":[OSD([sQuery(id+"F0.wireOp",EDGE,"E13")])]}),makeQuery(id+"F5.opExtrude","SWEPT_FACE",FACE,{"disambiguationData":[OSD([sQuery(id+"F4.wireOp",EDGE,"E34")])]})]})],"blendedInto":[makeQuery(id+"F5.boolean.opBoolean","MERGE",FACE,{"derivedFrom":[makeQuery(id+"F1.opExtrude","SWEPT_FACE",FACE,{"disambiguationData":[OSD([sQuery(id+"F0.wireOp",EDGE,"E13")])]}),makeQuery(id+"F5.opExtrude","SWEPT_FACE",FACE,{"disambiguationData":[OSD([sQuery(id+"F4.wireOp",EDGE,"E34")])]})]})]});
            var Q1;
            Q1=makeQuery(id+"F8.opChamfer","BLEND_EDGE",EDGE,{"blendedFrom":[makeQuery(id+"F1.opExtrude","CAP_EDGE",EDGE,{"disambiguationData":[OSD([sQuery(id+"F0.wireOp",EDGE,"E6")])],"isStart":false}),makeQuery(id+"F5.boolean.opBoolean","MERGE",FACE,{"derivedFrom":[makeQuery(id+"F1.opExtrude","SWEPT_FACE",FACE,{"disambiguationData":[OSD([sQuery(id+"F0.wireOp",EDGE,"E13")])]}),makeQuery(id+"F5.opExtrude","SWEPT_FACE",FACE,{"disambiguationData":[OSD([sQuery(id+"F4.wireOp",EDGE,"E34")])]})]})],"blendedInto":[makeQuery(id+"F5.boolean.opBoolean","MERGE",FACE,{"derivedFrom":[makeQuery(id+"F1.opExtrude","SWEPT_FACE",FACE,{"disambiguationData":[OSD([sQuery(id+"F0.wireOp",EDGE,"E13")])]}),makeQuery(id+"F5.opExtrude","SWEPT_FACE",FACE,{"disambiguationData":[OSD([sQuery(id+"F4.wireOp",EDGE,"E34")])]})]})]});
            var Q2;
            Q2=makeQuery(id+"F8.opChamfer","BLEND_EDGE",EDGE,{"blendedFrom":[makeQuery(id+"F1.opExtrude","CAP_EDGE",EDGE,{"disambiguationData":[OSD([sQuery(id+"F0.wireOp",EDGE,"E3")])],"isStart":false}),makeQuery(id+"F5.boolean.opBoolean","MERGE",FACE,{"derivedFrom":[makeQuery(id+"F1.opExtrude","SWEPT_FACE",FACE,{"disambiguationData":[OSD([sQuery(id+"F0.wireOp",EDGE,"E12")])]}),makeQuery(id+"F5.opExtrude","SWEPT_FACE",FACE,{"disambiguationData":[OSD([sQuery(id+"F4.wireOp",EDGE,"E33")])]})]})],"blendedInto":[makeQuery(id+"F5.boolean.opBoolean","MERGE",FACE,{"derivedFrom":[makeQuery(id+"F1.opExtrude","SWEPT_FACE",FACE,{"disambiguationData":[OSD([sQuery(id+"F0.wireOp",EDGE,"E12")])]}),makeQuery(id+"F5.opExtrude","SWEPT_FACE",FACE,{"disambiguationData":[OSD([sQuery(id+"F4.wireOp",EDGE,"E33")])]})]})]});
            var Q3;
            Q3=makeQuery(id+"F8.opChamfer","BLEND_EDGE",EDGE,{"blendedFrom":[makeQuery(id+"F1.opExtrude","CAP_EDGE",EDGE,{"disambiguationData":[OSD([sQuery(id+"F0.wireOp",EDGE,"E7")])],"isStart":false}),makeQuery(id+"F5.boolean.opBoolean","MERGE",FACE,{"derivedFrom":[makeQuery(id+"F1.opExtrude","SWEPT_FACE",FACE,{"disambiguationData":[OSD([sQuery(id+"F0.wireOp",EDGE,"E12")])]}),makeQuery(id+"F5.opExtrude","SWEPT_FACE",FACE,{"disambiguationData":[OSD([sQuery(id+"F4.wireOp",EDGE,"E33")])]})]})],"blendedInto":[makeQuery(id+"F5.boolean.opBoolean","MERGE",FACE,{"derivedFrom":[makeQuery(id+"F1.opExtrude","SWEPT_FACE",FACE,{"disambiguationData":[OSD([sQuery(id+"F0.wireOp",EDGE,"E12")])]}),makeQuery(id+"F5.opExtrude","SWEPT_FACE",FACE,{"disambiguationData":[OSD([sQuery(id+"F4.wireOp",EDGE,"E33")])]})]})]});
            var Q4;
            Q4=makeQuery(id+"F8.opChamfer","BLEND_EDGE",EDGE,{"blendedFrom":[makeQuery(id+"F1.opExtrude","CAP_EDGE",EDGE,{"disambiguationData":[OSD([sQuery(id+"F0.wireOp",EDGE,"E9")])],"isStart":false}),makeQuery(id+"F5.boolean.opBoolean","MERGE",FACE,{"derivedFrom":[makeQuery(id+"F1.opExtrude","SWEPT_FACE",FACE,{"disambiguationData":[OSD([sQuery(id+"F0.wireOp",EDGE,"E11")])]}),makeQuery(id+"F5.opExtrude","SWEPT_FACE",FACE,{"disambiguationData":[OSD([sQuery(id+"F4.wireOp",EDGE,"E32")])]})]})],"blendedInto":[makeQuery(id+"F5.boolean.opBoolean","MERGE",FACE,{"derivedFrom":[makeQuery(id+"F1.opExtrude","SWEPT_FACE",FACE,{"disambiguationData":[OSD([sQuery(id+"F0.wireOp",EDGE,"E11")])]}),makeQuery(id+"F5.opExtrude","SWEPT_FACE",FACE,{"disambiguationData":[OSD([sQuery(id+"F4.wireOp",EDGE,"E32")])]})]})]});
            var Q5;
            Q5=makeQuery(id+"F8.opChamfer","BLEND_EDGE",EDGE,{"blendedFrom":[makeQuery(id+"F1.opExtrude","CAP_EDGE",EDGE,{"disambiguationData":[OSD([sQuery(id+"F0.wireOp",EDGE,"E4")])],"isStart":false}),makeQuery(id+"F5.boolean.opBoolean","MERGE",FACE,{"derivedFrom":[makeQuery(id+"F1.opExtrude","SWEPT_FACE",FACE,{"disambiguationData":[OSD([sQuery(id+"F0.wireOp",EDGE,"E10")])]}),makeQuery(id+"F5.opExtrude","SWEPT_FACE",FACE,{"disambiguationData":[OSD([sQuery(id+"F4.wireOp",EDGE,"E31")])]})]})],"blendedInto":[makeQuery(id+"F5.boolean.opBoolean","MERGE",FACE,{"derivedFrom":[makeQuery(id+"F1.opExtrude","SWEPT_FACE",FACE,{"disambiguationData":[OSD([sQuery(id+"F0.wireOp",EDGE,"E10")])]}),makeQuery(id+"F5.opExtrude","SWEPT_FACE",FACE,{"disambiguationData":[OSD([sQuery(id+"F4.wireOp",EDGE,"E31")])]})]})]});
            var Q6;
            Q6=makeQuery(id+"F8.opChamfer","BLEND_EDGE",EDGE,{"blendedFrom":[makeQuery(id+"F1.opExtrude","CAP_EDGE",EDGE,{"disambiguationData":[OSD([sQuery(id+"F0.wireOp",EDGE,"E0")])],"isStart":false}),makeQuery(id+"F5.boolean.opBoolean","MERGE",FACE,{"derivedFrom":[makeQuery(id+"F1.opExtrude","SWEPT_FACE",FACE,{"disambiguationData":[OSD([sQuery(id+"F0.wireOp",EDGE,"E10")])]}),makeQuery(id+"F5.opExtrude","SWEPT_FACE",FACE,{"disambiguationData":[OSD([sQuery(id+"F4.wireOp",EDGE,"E31")])]})]})],"blendedInto":[makeQuery(id+"F5.boolean.opBoolean","MERGE",FACE,{"derivedFrom":[makeQuery(id+"F1.opExtrude","SWEPT_FACE",FACE,{"disambiguationData":[OSD([sQuery(id+"F0.wireOp",EDGE,"E10")])]}),makeQuery(id+"F5.opExtrude","SWEPT_FACE",FACE,{"disambiguationData":[OSD([sQuery(id+"F4.wireOp",EDGE,"E31")])]})]})]});
            var Q7;
            Q7=makeQuery(id+"F8.opChamfer","BLEND_EDGE",EDGE,{"blendedFrom":[makeQuery(id+"F1.opExtrude","CAP_EDGE",EDGE,{"disambiguationData":[OSD([sQuery(id+"F0.wireOp",EDGE,"E1")])],"isStart":false}),makeQuery(id+"F5.boolean.opBoolean","MERGE",FACE,{"derivedFrom":[makeQuery(id+"F1.opExtrude","SWEPT_FACE",FACE,{"disambiguationData":[OSD([sQuery(id+"F0.wireOp",EDGE,"E11")])]}),makeQuery(id+"F5.opExtrude","SWEPT_FACE",FACE,{"disambiguationData":[OSD([sQuery(id+"F4.wireOp",EDGE,"E32")])]})]})],"blendedInto":[makeQuery(id+"F5.boolean.opBoolean","MERGE",FACE,{"derivedFrom":[makeQuery(id+"F1.opExtrude","SWEPT_FACE",FACE,{"disambiguationData":[OSD([sQuery(id+"F0.wireOp",EDGE,"E11")])]}),makeQuery(id+"F5.opExtrude","SWEPT_FACE",FACE,{"disambiguationData":[OSD([sQuery(id+"F4.wireOp",EDGE,"E32")])]})]})]});
            fillet(context, id + "F13", {"entities" : qUnion([Q0, Q1, Q2, Q3, Q4, Q5, Q6, Q7]), "radius" : 13 * mm, "tangentPropagation" : true, "allowEdgeOverflow" : false});
        }
        {
            var Q0;
            {var subQ0=sQuery(id+"F0.wireOp",EDGE,"E1");var subQ1=sQuery(id+"F0.wireOp",EDGE,"E0");var subQ2=makeQuery(id+"F1.opExtrude","CAP_FACE",FACE,{"disambiguationData":[OSD([subQ1,subQ0,sQuery(id+"F0.wireOp",EDGE,"E2"),sQuery(id+"F0.wireOp",EDGE,"E3"),sQuery(id+"F0.wireOp",EDGE,"E4"),sQuery(id+"F0.wireOp",EDGE,"E5"),sQuery(id+"F0.wireOp",EDGE,"E6"),sQuery(id+"F0.wireOp",EDGE,"E7"),sQuery(id+"F0.wireOp",EDGE,"E8"),sQuery(id+"F0.wireOp",EDGE,"E9"),sQuery(id+"F0.wireOp",EDGE,"E10"),sQuery(id+"F0.wireOp",EDGE,"E11"),sQuery(id+"F0.wireOp",EDGE,"E12"),sQuery(id+"F0.wireOp",EDGE,"E13"),sQuery(id+"F0.wireOp",EDGE,"E14"),sQuery(id+"F0.wireOp",EDGE,"E15"),sQuery(id+"F0.wireOp",EDGE,"E16"),sQuery(id+"F0.wireOp",EDGE,"E17"),sQuery(id+"F0.wireOp",EDGE,"E18"),sQuery(id+"F0.wireOp",EDGE,"E19"),sQuery(id+"F0.wireOp",EDGE,"E20"),sQuery(id+"F0.wireOp",EDGE,"E21"),sQuery(id+"F0.wireOp",EDGE,"E22.filletArc"),sQuery(id+"F0.wireOp",EDGE,"E23.filletArc"),sQuery(id+"F0.wireOp",EDGE,"E24.filletArc"),sQuery(id+"F0.wireOp",EDGE,"E25.filletArc"),sQuery(id+"F0.wireOp",EDGE,"E26.filletArc"),sQuery(id+"F0.wireOp",EDGE,"E27.filletArc"),sQuery(id+"F0.wireOp",EDGE,"E28.filletArc"),sQuery(id+"F0.wireOp",EDGE,"E29.filletArc")])],"isStart":false});Q0=makeQuery(id+"F8.opChamfer","BLEND_EDGE",EDGE,{"blendedFrom":[makeQuery(id+"F6.opFillet","BLEND_EDGE",EDGE,{"blendedFrom":[makeQuery(id+"F1.opExtrude","SWEPT_EDGE",EDGE,{"disambiguationData":[OSD([subQ1,subQ0])]}),subQ2],"blendedInto":[subQ2]}),subQ2],"blendedInto":[subQ2]});}
            var Q1;
            {var subQ0=sQuery(id+"F0.wireOp",EDGE,"E5");var subQ1=sQuery(id+"F0.wireOp",EDGE,"E4");var subQ2=makeQuery(id+"F1.opExtrude","CAP_FACE",FACE,{"disambiguationData":[OSD([sQuery(id+"F0.wireOp",EDGE,"E0"),sQuery(id+"F0.wireOp",EDGE,"E1"),sQuery(id+"F0.wireOp",EDGE,"E2"),sQuery(id+"F0.wireOp",EDGE,"E3"),subQ1,subQ0,sQuery(id+"F0.wireOp",EDGE,"E6"),sQuery(id+"F0.wireOp",EDGE,"E7"),sQuery(id+"F0.wireOp",EDGE,"E8"),sQuery(id+"F0.wireOp",EDGE,"E9"),sQuery(id+"F0.wireOp",EDGE,"E10"),sQuery(id+"F0.wireOp",EDGE,"E11"),sQuery(id+"F0.wireOp",EDGE,"E12"),sQuery(id+"F0.wireOp",EDGE,"E13"),sQuery(id+"F0.wireOp",EDGE,"E14"),sQuery(id+"F0.wireOp",EDGE,"E15"),sQuery(id+"F0.wireOp",EDGE,"E16"),sQuery(id+"F0.wireOp",EDGE,"E17"),sQuery(id+"F0.wireOp",EDGE,"E18"),sQuery(id+"F0.wireOp",EDGE,"E19"),sQuery(id+"F0.wireOp",EDGE,"E20"),sQuery(id+"F0.wireOp",EDGE,"E21"),sQuery(id+"F0.wireOp",EDGE,"E22.filletArc"),sQuery(id+"F0.wireOp",EDGE,"E23.filletArc"),sQuery(id+"F0.wireOp",EDGE,"E24.filletArc"),sQuery(id+"F0.wireOp",EDGE,"E25.filletArc"),sQuery(id+"F0.wireOp",EDGE,"E26.filletArc"),sQuery(id+"F0.wireOp",EDGE,"E27.filletArc"),sQuery(id+"F0.wireOp",EDGE,"E28.filletArc"),sQuery(id+"F0.wireOp",EDGE,"E29.filletArc")])],"isStart":false});Q1=makeQuery(id+"F8.opChamfer","BLEND_EDGE",EDGE,{"blendedFrom":[makeQuery(id+"F7.opFillet","BLEND_EDGE",EDGE,{"blendedFrom":[makeQuery(id+"F1.opExtrude","SWEPT_EDGE",EDGE,{"disambiguationData":[OSD([subQ1,subQ0])]}),subQ2],"blendedInto":[subQ2]}),subQ2],"blendedInto":[subQ2]});}
            var Q2;
            {var subQ0=sQuery(id+"F0.wireOp",EDGE,"E3");var subQ1=sQuery(id+"F0.wireOp",EDGE,"E2");var subQ2=makeQuery(id+"F1.opExtrude","CAP_FACE",FACE,{"disambiguationData":[OSD([sQuery(id+"F0.wireOp",EDGE,"E0"),sQuery(id+"F0.wireOp",EDGE,"E1"),subQ1,subQ0,sQuery(id+"F0.wireOp",EDGE,"E4"),sQuery(id+"F0.wireOp",EDGE,"E5"),sQuery(id+"F0.wireOp",EDGE,"E6"),sQuery(id+"F0.wireOp",EDGE,"E7"),sQuery(id+"F0.wireOp",EDGE,"E8"),sQuery(id+"F0.wireOp",EDGE,"E9"),sQuery(id+"F0.wireOp",EDGE,"E10"),sQuery(id+"F0.wireOp",EDGE,"E11"),sQuery(id+"F0.wireOp",EDGE,"E12"),sQuery(id+"F0.wireOp",EDGE,"E13"),sQuery(id+"F0.wireOp",EDGE,"E14"),sQuery(id+"F0.wireOp",EDGE,"E15"),sQuery(id+"F0.wireOp",EDGE,"E16"),sQuery(id+"F0.wireOp",EDGE,"E17"),sQuery(id+"F0.wireOp",EDGE,"E18"),sQuery(id+"F0.wireOp",EDGE,"E19"),sQuery(id+"F0.wireOp",EDGE,"E20"),sQuery(id+"F0.wireOp",EDGE,"E21"),sQuery(id+"F0.wireOp",EDGE,"E22.filletArc"),sQuery(id+"F0.wireOp",EDGE,"E23.filletArc"),sQuery(id+"F0.wireOp",EDGE,"E24.filletArc"),sQuery(id+"F0.wireOp",EDGE,"E25.filletArc"),sQuery(id+"F0.wireOp",EDGE,"E26.filletArc"),sQuery(id+"F0.wireOp",EDGE,"E27.filletArc"),sQuery(id+"F0.wireOp",EDGE,"E28.filletArc"),sQuery(id+"F0.wireOp",EDGE,"E29.filletArc")])],"isStart":false});Q2=makeQuery(id+"F8.opChamfer","BLEND_EDGE",EDGE,{"blendedFrom":[makeQuery(id+"F6.opFillet","BLEND_EDGE",EDGE,{"blendedFrom":[makeQuery(id+"F1.opExtrude","SWEPT_EDGE",EDGE,{"disambiguationData":[OSD([subQ1,subQ0])]}),subQ2],"blendedInto":[subQ2]}),subQ2],"blendedInto":[subQ2]});}
            var Q3;
            {var subQ0=sQuery(id+"F0.wireOp",EDGE,"E8");Q3=makeQuery(id+"F8.opChamfer","BLEND_EDGE",EDGE,{"blendedFrom":[makeQuery(id+"F1.opExtrude","CAP_EDGE",EDGE,{"disambiguationData":[OSD([subQ0])],"isStart":false}),makeQuery(id+"F1.opExtrude","CAP_FACE",FACE,{"disambiguationData":[OSD([sQuery(id+"F0.wireOp",EDGE,"E0"),sQuery(id+"F0.wireOp",EDGE,"E1"),sQuery(id+"F0.wireOp",EDGE,"E2"),sQuery(id+"F0.wireOp",EDGE,"E3"),sQuery(id+"F0.wireOp",EDGE,"E4"),sQuery(id+"F0.wireOp",EDGE,"E5"),sQuery(id+"F0.wireOp",EDGE,"E6"),sQuery(id+"F0.wireOp",EDGE,"E7"),subQ0,sQuery(id+"F0.wireOp",EDGE,"E9"),sQuery(id+"F0.wireOp",EDGE,"E10"),sQuery(id+"F0.wireOp",EDGE,"E11"),sQuery(id+"F0.wireOp",EDGE,"E12"),sQuery(id+"F0.wireOp",EDGE,"E13"),sQuery(id+"F0.wireOp",EDGE,"E14"),sQuery(id+"F0.wireOp",EDGE,"E15"),sQuery(id+"F0.wireOp",EDGE,"E16"),sQuery(id+"F0.wireOp",EDGE,"E17"),sQuery(id+"F0.wireOp",EDGE,"E18"),sQuery(id+"F0.wireOp",EDGE,"E19"),sQuery(id+"F0.wireOp",EDGE,"E20"),sQuery(id+"F0.wireOp",EDGE,"E21"),sQuery(id+"F0.wireOp",EDGE,"E22.filletArc"),sQuery(id+"F0.wireOp",EDGE,"E23.filletArc"),sQuery(id+"F0.wireOp",EDGE,"E24.filletArc"),sQuery(id+"F0.wireOp",EDGE,"E25.filletArc"),sQuery(id+"F0.wireOp",EDGE,"E26.filletArc"),sQuery(id+"F0.wireOp",EDGE,"E27.filletArc"),sQuery(id+"F0.wireOp",EDGE,"E28.filletArc"),sQuery(id+"F0.wireOp",EDGE,"E29.filletArc")])],"isStart":false})],"blendedInto":[makeQuery(id+"F1.opExtrude","CAP_FACE",FACE,{"disambiguationData":[OSD([sQuery(id+"F0.wireOp",EDGE,"E0"),sQuery(id+"F0.wireOp",EDGE,"E1"),sQuery(id+"F0.wireOp",EDGE,"E2"),sQuery(id+"F0.wireOp",EDGE,"E3"),sQuery(id+"F0.wireOp",EDGE,"E4"),sQuery(id+"F0.wireOp",EDGE,"E5"),sQuery(id+"F0.wireOp",EDGE,"E6"),sQuery(id+"F0.wireOp",EDGE,"E7"),subQ0,sQuery(id+"F0.wireOp",EDGE,"E9"),sQuery(id+"F0.wireOp",EDGE,"E10"),sQuery(id+"F0.wireOp",EDGE,"E11"),sQuery(id+"F0.wireOp",EDGE,"E12"),sQuery(id+"F0.wireOp",EDGE,"E13"),sQuery(id+"F0.wireOp",EDGE,"E14"),sQuery(id+"F0.wireOp",EDGE,"E15"),sQuery(id+"F0.wireOp",EDGE,"E16"),sQuery(id+"F0.wireOp",EDGE,"E17"),sQuery(id+"F0.wireOp",EDGE,"E18"),sQuery(id+"F0.wireOp",EDGE,"E19"),sQuery(id+"F0.wireOp",EDGE,"E20"),sQuery(id+"F0.wireOp",EDGE,"E21"),sQuery(id+"F0.wireOp",EDGE,"E22.filletArc"),sQuery(id+"F0.wireOp",EDGE,"E23.filletArc"),sQuery(id+"F0.wireOp",EDGE,"E24.filletArc"),sQuery(id+"F0.wireOp",EDGE,"E25.filletArc"),sQuery(id+"F0.wireOp",EDGE,"E26.filletArc"),sQuery(id+"F0.wireOp",EDGE,"E27.filletArc"),sQuery(id+"F0.wireOp",EDGE,"E28.filletArc"),sQuery(id+"F0.wireOp",EDGE,"E29.filletArc")])],"isStart":false})]});}
            fillet(context, id + "F14", {"entities" : qUnion([Q0, Q1, Q2, Q3]), "radius" : .7 * mm, "tangentPropagation" : true, "allowEdgeOverflow" : false});
        }
        {
            var Q0;
            {var subQ0=makeQuery(id+"F1.opExtrude","CAP_FACE",FACE,{"disambiguationData":[OSD([sQuery(id+"F0.wireOp",EDGE,"E0"),sQuery(id+"F0.wireOp",EDGE,"E1"),sQuery(id+"F0.wireOp",EDGE,"E2"),sQuery(id+"F0.wireOp",EDGE,"E3"),sQuery(id+"F0.wireOp",EDGE,"E4"),sQuery(id+"F0.wireOp",EDGE,"E5"),sQuery(id+"F0.wireOp",EDGE,"E6"),sQuery(id+"F0.wireOp",EDGE,"E7"),sQuery(id+"F0.wireOp",EDGE,"E8"),sQuery(id+"F0.wireOp",EDGE,"E9"),sQuery(id+"F0.wireOp",EDGE,"E10"),sQuery(id+"F0.wireOp",EDGE,"E11"),sQuery(id+"F0.wireOp",EDGE,"E12"),sQuery(id+"F0.wireOp",EDGE,"E13"),sQuery(id+"F0.wireOp",EDGE,"E14"),sQuery(id+"F0.wireOp",EDGE,"E15"),sQuery(id+"F0.wireOp",EDGE,"E16"),sQuery(id+"F0.wireOp",EDGE,"E17"),sQuery(id+"F0.wireOp",EDGE,"E18"),sQuery(id+"F0.wireOp",EDGE,"E19"),sQuery(id+"F0.wireOp",EDGE,"E20"),sQuery(id+"F0.wireOp",EDGE,"E21"),sQuery(id+"F0.wireOp",EDGE,"E22.filletArc"),sQuery(id+"F0.wireOp",EDGE,"E23.filletArc"),sQuery(id+"F0.wireOp",EDGE,"E24.filletArc"),sQuery(id+"F0.wireOp",EDGE,"E25.filletArc"),sQuery(id+"F0.wireOp",EDGE,"E26.filletArc"),sQuery(id+"F0.wireOp",EDGE,"E27.filletArc"),sQuery(id+"F0.wireOp",EDGE,"E28.filletArc"),sQuery(id+"F0.wireOp",EDGE,"E29.filletArc")])],"isStart":false});Q0=makeQuery(id+"F10.opChamfer","BLEND_EDGE",EDGE,{"blendedFrom":[makeQuery(id+"F3.boolean.opBoolean","INTERSECT",EDGE,{"derivedFrom":[subQ0,makeQuery(id+"F3.opExtrude","CAP_FACE",FACE,{"disambiguationData":[OSD([sQuery(id+"F2.wireOp",EDGE,"E30.bottom"),sQuery(id+"F2.wireOp",EDGE,"E30.top"),sQuery(id+"F2.wireOp",EDGE,"E30.left"),sQuery(id+"F2.wireOp",EDGE,"E30.right")])],"isStart":false})]}),subQ0],"blendedInto":[subQ0]});}
            fillet(context, id + "F15", {"entities" : qUnion([Q0]), "radius" : .7 * mm, "tangentPropagation" : true, "allowEdgeOverflow" : false});
        }
        {
            var Q0;
            Q0=makeQuery(id+"F5.opExtrude","CAP_FACE",FACE,{"disambiguationData":[OSD([sQuery(id+"F4.wireOp",EDGE,"E31")])],"isStart":false});
            var Q1;
            Q1=makeQuery(id+"F5.opExtrude","CAP_FACE",FACE,{"disambiguationData":[OSD([sQuery(id+"F4.wireOp",EDGE,"E34")])],"isStart":false});
            var Q2;
            Q2=makeQuery(id+"F5.opExtrude","CAP_FACE",FACE,{"disambiguationData":[OSD([sQuery(id+"F4.wireOp",EDGE,"E33")])],"isStart":false});
            var Q3;
            Q3=makeQuery(id+"F5.opExtrude","CAP_FACE",FACE,{"disambiguationData":[OSD([sQuery(id+"F4.wireOp",EDGE,"E32")])],"isStart":false});
            fillet(context, id + "F16", {"entities" : qUnion([Q0, Q1, Q2, Q3]), "radius" : 3 * mm, "tangentPropagation" : true, "allowEdgeOverflow" : false});
        }
        {
            var Q0;
            Q0=makeQuery(id+"F16.opFillet","BLEND_EDGE",EDGE,{"blendedFrom":[makeQuery(id+"F5.opExtrude","CAP_EDGE",EDGE,{"disambiguationData":[OSD([sQuery(id+"F4.wireOp",EDGE,"E34")])],"isStart":false}),makeQuery(id+"F1.opExtrude","CAP_FACE",FACE,{"disambiguationData":[OSD([sQuery(id+"F0.wireOp",EDGE,"E0"),sQuery(id+"F0.wireOp",EDGE,"E1"),sQuery(id+"F0.wireOp",EDGE,"E2"),sQuery(id+"F0.wireOp",EDGE,"E3"),sQuery(id+"F0.wireOp",EDGE,"E4"),sQuery(id+"F0.wireOp",EDGE,"E5"),sQuery(id+"F0.wireOp",EDGE,"E6"),sQuery(id+"F0.wireOp",EDGE,"E7"),sQuery(id+"F0.wireOp",EDGE,"E8"),sQuery(id+"F0.wireOp",EDGE,"E9"),sQuery(id+"F0.wireOp",EDGE,"E10"),sQuery(id+"F0.wireOp",EDGE,"E11"),sQuery(id+"F0.wireOp",EDGE,"E12"),sQuery(id+"F0.wireOp",EDGE,"E13"),sQuery(id+"F0.wireOp",EDGE,"E14"),sQuery(id+"F0.wireOp",EDGE,"E15"),sQuery(id+"F0.wireOp",EDGE,"E16"),sQuery(id+"F0.wireOp",EDGE,"E17"),sQuery(id+"F0.wireOp",EDGE,"E18"),sQuery(id+"F0.wireOp",EDGE,"E19"),sQuery(id+"F0.wireOp",EDGE,"E20"),sQuery(id+"F0.wireOp",EDGE,"E21"),sQuery(id+"F0.wireOp",EDGE,"E22.filletArc"),sQuery(id+"F0.wireOp",EDGE,"E23.filletArc"),sQuery(id+"F0.wireOp",EDGE,"E24.filletArc"),sQuery(id+"F0.wireOp",EDGE,"E25.filletArc"),sQuery(id+"F0.wireOp",EDGE,"E26.filletArc"),sQuery(id+"F0.wireOp",EDGE,"E27.filletArc"),sQuery(id+"F0.wireOp",EDGE,"E28.filletArc"),sQuery(id+"F0.wireOp",EDGE,"E29.filletArc")])],"isStart":false})],"blendedInto":[makeQuery(id+"F1.opExtrude","CAP_FACE",FACE,{"disambiguationData":[OSD([sQuery(id+"F0.wireOp",EDGE,"E0"),sQuery(id+"F0.wireOp",EDGE,"E1"),sQuery(id+"F0.wireOp",EDGE,"E2"),sQuery(id+"F0.wireOp",EDGE,"E3"),sQuery(id+"F0.wireOp",EDGE,"E4"),sQuery(id+"F0.wireOp",EDGE,"E5"),sQuery(id+"F0.wireOp",EDGE,"E6"),sQuery(id+"F0.wireOp",EDGE,"E7"),sQuery(id+"F0.wireOp",EDGE,"E8"),sQuery(id+"F0.wireOp",EDGE,"E9"),sQuery(id+"F0.wireOp",EDGE,"E10"),sQuery(id+"F0.wireOp",EDGE,"E11"),sQuery(id+"F0.wireOp",EDGE,"E12"),sQuery(id+"F0.wireOp",EDGE,"E13"),sQuery(id+"F0.wireOp",EDGE,"E14"),sQuery(id+"F0.wireOp",EDGE,"E15"),sQuery(id+"F0.wireOp",EDGE,"E16"),sQuery(id+"F0.wireOp",EDGE,"E17"),sQuery(id+"F0.wireOp",EDGE,"E18"),sQuery(id+"F0.wireOp",EDGE,"E19"),sQuery(id+"F0.wireOp",EDGE,"E20"),sQuery(id+"F0.wireOp",EDGE,"E21"),sQuery(id+"F0.wireOp",EDGE,"E22.filletArc"),sQuery(id+"F0.wireOp",EDGE,"E23.filletArc"),sQuery(id+"F0.wireOp",EDGE,"E24.filletArc"),sQuery(id+"F0.wireOp",EDGE,"E25.filletArc"),sQuery(id+"F0.wireOp",EDGE,"E26.filletArc"),sQuery(id+"F0.wireOp",EDGE,"E27.filletArc"),sQuery(id+"F0.wireOp",EDGE,"E28.filletArc"),sQuery(id+"F0.wireOp",EDGE,"E29.filletArc")])],"isStart":false})]});
            var Q1;
            Q1=makeQuery(id+"F16.opFillet","BLEND_EDGE",EDGE,{"blendedFrom":[makeQuery(id+"F5.opExtrude","CAP_EDGE",EDGE,{"disambiguationData":[OSD([sQuery(id+"F4.wireOp",EDGE,"E33")])],"isStart":false}),makeQuery(id+"F1.opExtrude","CAP_FACE",FACE,{"disambiguationData":[OSD([sQuery(id+"F0.wireOp",EDGE,"E0"),sQuery(id+"F0.wireOp",EDGE,"E1"),sQuery(id+"F0.wireOp",EDGE,"E2"),sQuery(id+"F0.wireOp",EDGE,"E3"),sQuery(id+"F0.wireOp",EDGE,"E4"),sQuery(id+"F0.wireOp",EDGE,"E5"),sQuery(id+"F0.wireOp",EDGE,"E6"),sQuery(id+"F0.wireOp",EDGE,"E7"),sQuery(id+"F0.wireOp",EDGE,"E8"),sQuery(id+"F0.wireOp",EDGE,"E9"),sQuery(id+"F0.wireOp",EDGE,"E10"),sQuery(id+"F0.wireOp",EDGE,"E11"),sQuery(id+"F0.wireOp",EDGE,"E12"),sQuery(id+"F0.wireOp",EDGE,"E13"),sQuery(id+"F0.wireOp",EDGE,"E14"),sQuery(id+"F0.wireOp",EDGE,"E15"),sQuery(id+"F0.wireOp",EDGE,"E16"),sQuery(id+"F0.wireOp",EDGE,"E17"),sQuery(id+"F0.wireOp",EDGE,"E18"),sQuery(id+"F0.wireOp",EDGE,"E19"),sQuery(id+"F0.wireOp",EDGE,"E20"),sQuery(id+"F0.wireOp",EDGE,"E21"),sQuery(id+"F0.wireOp",EDGE,"E22.filletArc"),sQuery(id+"F0.wireOp",EDGE,"E23.filletArc"),sQuery(id+"F0.wireOp",EDGE,"E24.filletArc"),sQuery(id+"F0.wireOp",EDGE,"E25.filletArc"),sQuery(id+"F0.wireOp",EDGE,"E26.filletArc"),sQuery(id+"F0.wireOp",EDGE,"E27.filletArc"),sQuery(id+"F0.wireOp",EDGE,"E28.filletArc"),sQuery(id+"F0.wireOp",EDGE,"E29.filletArc")])],"isStart":false})],"blendedInto":[makeQuery(id+"F1.opExtrude","CAP_FACE",FACE,{"disambiguationData":[OSD([sQuery(id+"F0.wireOp",EDGE,"E0"),sQuery(id+"F0.wireOp",EDGE,"E1"),sQuery(id+"F0.wireOp",EDGE,"E2"),sQuery(id+"F0.wireOp",EDGE,"E3"),sQuery(id+"F0.wireOp",EDGE,"E4"),sQuery(id+"F0.wireOp",EDGE,"E5"),sQuery(id+"F0.wireOp",EDGE,"E6"),sQuery(id+"F0.wireOp",EDGE,"E7"),sQuery(id+"F0.wireOp",EDGE,"E8"),sQuery(id+"F0.wireOp",EDGE,"E9"),sQuery(id+"F0.wireOp",EDGE,"E10"),sQuery(id+"F0.wireOp",EDGE,"E11"),sQuery(id+"F0.wireOp",EDGE,"E12"),sQuery(id+"F0.wireOp",EDGE,"E13"),sQuery(id+"F0.wireOp",EDGE,"E14"),sQuery(id+"F0.wireOp",EDGE,"E15"),sQuery(id+"F0.wireOp",EDGE,"E16"),sQuery(id+"F0.wireOp",EDGE,"E17"),sQuery(id+"F0.wireOp",EDGE,"E18"),sQuery(id+"F0.wireOp",EDGE,"E19"),sQuery(id+"F0.wireOp",EDGE,"E20"),sQuery(id+"F0.wireOp",EDGE,"E21"),sQuery(id+"F0.wireOp",EDGE,"E22.filletArc"),sQuery(id+"F0.wireOp",EDGE,"E23.filletArc"),sQuery(id+"F0.wireOp",EDGE,"E24.filletArc"),sQuery(id+"F0.wireOp",EDGE,"E25.filletArc"),sQuery(id+"F0.wireOp",EDGE,"E26.filletArc"),sQuery(id+"F0.wireOp",EDGE,"E27.filletArc"),sQuery(id+"F0.wireOp",EDGE,"E28.filletArc"),sQuery(id+"F0.wireOp",EDGE,"E29.filletArc")])],"isStart":false})]});
            var Q2;
            Q2=makeQuery(id+"F16.opFillet","BLEND_EDGE",EDGE,{"blendedFrom":[makeQuery(id+"F5.opExtrude","CAP_EDGE",EDGE,{"disambiguationData":[OSD([sQuery(id+"F4.wireOp",EDGE,"E32")])],"isStart":false}),makeQuery(id+"F1.opExtrude","CAP_FACE",FACE,{"disambiguationData":[OSD([sQuery(id+"F0.wireOp",EDGE,"E0"),sQuery(id+"F0.wireOp",EDGE,"E1"),sQuery(id+"F0.wireOp",EDGE,"E2"),sQuery(id+"F0.wireOp",EDGE,"E3"),sQuery(id+"F0.wireOp",EDGE,"E4"),sQuery(id+"F0.wireOp",EDGE,"E5"),sQuery(id+"F0.wireOp",EDGE,"E6"),sQuery(id+"F0.wireOp",EDGE,"E7"),sQuery(id+"F0.wireOp",EDGE,"E8"),sQuery(id+"F0.wireOp",EDGE,"E9"),sQuery(id+"F0.wireOp",EDGE,"E10"),sQuery(id+"F0.wireOp",EDGE,"E11"),sQuery(id+"F0.wireOp",EDGE,"E12"),sQuery(id+"F0.wireOp",EDGE,"E13"),sQuery(id+"F0.wireOp",EDGE,"E14"),sQuery(id+"F0.wireOp",EDGE,"E15"),sQuery(id+"F0.wireOp",EDGE,"E16"),sQuery(id+"F0.wireOp",EDGE,"E17"),sQuery(id+"F0.wireOp",EDGE,"E18"),sQuery(id+"F0.wireOp",EDGE,"E19"),sQuery(id+"F0.wireOp",EDGE,"E20"),sQuery(id+"F0.wireOp",EDGE,"E21"),sQuery(id+"F0.wireOp",EDGE,"E22.filletArc"),sQuery(id+"F0.wireOp",EDGE,"E23.filletArc"),sQuery(id+"F0.wireOp",EDGE,"E24.filletArc"),sQuery(id+"F0.wireOp",EDGE,"E25.filletArc"),sQuery(id+"F0.wireOp",EDGE,"E26.filletArc"),sQuery(id+"F0.wireOp",EDGE,"E27.filletArc"),sQuery(id+"F0.wireOp",EDGE,"E28.filletArc"),sQuery(id+"F0.wireOp",EDGE,"E29.filletArc")])],"isStart":false})],"blendedInto":[makeQuery(id+"F1.opExtrude","CAP_FACE",FACE,{"disambiguationData":[OSD([sQuery(id+"F0.wireOp",EDGE,"E0"),sQuery(id+"F0.wireOp",EDGE,"E1"),sQuery(id+"F0.wireOp",EDGE,"E2"),sQuery(id+"F0.wireOp",EDGE,"E3"),sQuery(id+"F0.wireOp",EDGE,"E4"),sQuery(id+"F0.wireOp",EDGE,"E5"),sQuery(id+"F0.wireOp",EDGE,"E6"),sQuery(id+"F0.wireOp",EDGE,"E7"),sQuery(id+"F0.wireOp",EDGE,"E8"),sQuery(id+"F0.wireOp",EDGE,"E9"),sQuery(id+"F0.wireOp",EDGE,"E10"),sQuery(id+"F0.wireOp",EDGE,"E11"),sQuery(id+"F0.wireOp",EDGE,"E12"),sQuery(id+"F0.wireOp",EDGE,"E13"),sQuery(id+"F0.wireOp",EDGE,"E14"),sQuery(id+"F0.wireOp",EDGE,"E15"),sQuery(id+"F0.wireOp",EDGE,"E16"),sQuery(id+"F0.wireOp",EDGE,"E17"),sQuery(id+"F0.wireOp",EDGE,"E18"),sQuery(id+"F0.wireOp",EDGE,"E19"),sQuery(id+"F0.wireOp",EDGE,"E20"),sQuery(id+"F0.wireOp",EDGE,"E21"),sQuery(id+"F0.wireOp",EDGE,"E22.filletArc"),sQuery(id+"F0.wireOp",EDGE,"E23.filletArc"),sQuery(id+"F0.wireOp",EDGE,"E24.filletArc"),sQuery(id+"F0.wireOp",EDGE,"E25.filletArc"),sQuery(id+"F0.wireOp",EDGE,"E26.filletArc"),sQuery(id+"F0.wireOp",EDGE,"E27.filletArc"),sQuery(id+"F0.wireOp",EDGE,"E28.filletArc"),sQuery(id+"F0.wireOp",EDGE,"E29.filletArc")])],"isStart":false})]});
            var Q3;
            Q3=makeQuery(id+"F16.opFillet","BLEND_EDGE",EDGE,{"blendedFrom":[makeQuery(id+"F5.opExtrude","CAP_EDGE",EDGE,{"disambiguationData":[OSD([sQuery(id+"F4.wireOp",EDGE,"E31")])],"isStart":false}),makeQuery(id+"F1.opExtrude","CAP_FACE",FACE,{"disambiguationData":[OSD([sQuery(id+"F0.wireOp",EDGE,"E0"),sQuery(id+"F0.wireOp",EDGE,"E1"),sQuery(id+"F0.wireOp",EDGE,"E2"),sQuery(id+"F0.wireOp",EDGE,"E3"),sQuery(id+"F0.wireOp",EDGE,"E4"),sQuery(id+"F0.wireOp",EDGE,"E5"),sQuery(id+"F0.wireOp",EDGE,"E6"),sQuery(id+"F0.wireOp",EDGE,"E7"),sQuery(id+"F0.wireOp",EDGE,"E8"),sQuery(id+"F0.wireOp",EDGE,"E9"),sQuery(id+"F0.wireOp",EDGE,"E10"),sQuery(id+"F0.wireOp",EDGE,"E11"),sQuery(id+"F0.wireOp",EDGE,"E12"),sQuery(id+"F0.wireOp",EDGE,"E13"),sQuery(id+"F0.wireOp",EDGE,"E14"),sQuery(id+"F0.wireOp",EDGE,"E15"),sQuery(id+"F0.wireOp",EDGE,"E16"),sQuery(id+"F0.wireOp",EDGE,"E17"),sQuery(id+"F0.wireOp",EDGE,"E18"),sQuery(id+"F0.wireOp",EDGE,"E19"),sQuery(id+"F0.wireOp",EDGE,"E20"),sQuery(id+"F0.wireOp",EDGE,"E21"),sQuery(id+"F0.wireOp",EDGE,"E22.filletArc"),sQuery(id+"F0.wireOp",EDGE,"E23.filletArc"),sQuery(id+"F0.wireOp",EDGE,"E24.filletArc"),sQuery(id+"F0.wireOp",EDGE,"E25.filletArc"),sQuery(id+"F0.wireOp",EDGE,"E26.filletArc"),sQuery(id+"F0.wireOp",EDGE,"E27.filletArc"),sQuery(id+"F0.wireOp",EDGE,"E28.filletArc"),sQuery(id+"F0.wireOp",EDGE,"E29.filletArc")])],"isStart":false})],"blendedInto":[makeQuery(id+"F1.opExtrude","CAP_FACE",FACE,{"disambiguationData":[OSD([sQuery(id+"F0.wireOp",EDGE,"E0"),sQuery(id+"F0.wireOp",EDGE,"E1"),sQuery(id+"F0.wireOp",EDGE,"E2"),sQuery(id+"F0.wireOp",EDGE,"E3"),sQuery(id+"F0.wireOp",EDGE,"E4"),sQuery(id+"F0.wireOp",EDGE,"E5"),sQuery(id+"F0.wireOp",EDGE,"E6"),sQuery(id+"F0.wireOp",EDGE,"E7"),sQuery(id+"F0.wireOp",EDGE,"E8"),sQuery(id+"F0.wireOp",EDGE,"E9"),sQuery(id+"F0.wireOp",EDGE,"E10"),sQuery(id+"F0.wireOp",EDGE,"E11"),sQuery(id+"F0.wireOp",EDGE,"E12"),sQuery(id+"F0.wireOp",EDGE,"E13"),sQuery(id+"F0.wireOp",EDGE,"E14"),sQuery(id+"F0.wireOp",EDGE,"E15"),sQuery(id+"F0.wireOp",EDGE,"E16"),sQuery(id+"F0.wireOp",EDGE,"E17"),sQuery(id+"F0.wireOp",EDGE,"E18"),sQuery(id+"F0.wireOp",EDGE,"E19"),sQuery(id+"F0.wireOp",EDGE,"E20"),sQuery(id+"F0.wireOp",EDGE,"E21"),sQuery(id+"F0.wireOp",EDGE,"E22.filletArc"),sQuery(id+"F0.wireOp",EDGE,"E23.filletArc"),sQuery(id+"F0.wireOp",EDGE,"E24.filletArc"),sQuery(id+"F0.wireOp",EDGE,"E25.filletArc"),sQuery(id+"F0.wireOp",EDGE,"E26.filletArc"),sQuery(id+"F0.wireOp",EDGE,"E27.filletArc"),sQuery(id+"F0.wireOp",EDGE,"E28.filletArc"),sQuery(id+"F0.wireOp",EDGE,"E29.filletArc")])],"isStart":false})]});
            fillet(context, id + "F17", {"entities" : qUnion([Q0, Q1, Q2, Q3]), "radius" : 5 * mm, "tangentPropagation" : true, "allowEdgeOverflow" : false});
        }
        {
            var Q0;
            {var subQ0=sQuery(id+"F2.wireOp",EDGE,"E30.top");Q0=makeQuery(id+"F10.opChamfer","BLEND_EDGE",EDGE,{"blendedFrom":[makeQuery(id+"F3.boolean.opBoolean","INTERSECT",EDGE,{"derivedFrom":[makeQuery(id+"F1.opExtrude","CAP_FACE",FACE,{"disambiguationData":[OSD([sQuery(id+"F0.wireOp",EDGE,"E0"),sQuery(id+"F0.wireOp",EDGE,"E1"),sQuery(id+"F0.wireOp",EDGE,"E2"),sQuery(id+"F0.wireOp",EDGE,"E3"),sQuery(id+"F0.wireOp",EDGE,"E4"),sQuery(id+"F0.wireOp",EDGE,"E5"),sQuery(id+"F0.wireOp",EDGE,"E6"),sQuery(id+"F0.wireOp",EDGE,"E7"),sQuery(id+"F0.wireOp",EDGE,"E8"),sQuery(id+"F0.wireOp",EDGE,"E9"),sQuery(id+"F0.wireOp",EDGE,"E10"),sQuery(id+"F0.wireOp",EDGE,"E11"),sQuery(id+"F0.wireOp",EDGE,"E12"),sQuery(id+"F0.wireOp",EDGE,"E13"),sQuery(id+"F0.wireOp",EDGE,"E14"),sQuery(id+"F0.wireOp",EDGE,"E15"),sQuery(id+"F0.wireOp",EDGE,"E16"),sQuery(id+"F0.wireOp",EDGE,"E17"),sQuery(id+"F0.wireOp",EDGE,"E18"),sQuery(id+"F0.wireOp",EDGE,"E19"),sQuery(id+"F0.wireOp",EDGE,"E20"),sQuery(id+"F0.wireOp",EDGE,"E21"),sQuery(id+"F0.wireOp",EDGE,"E22.filletArc"),sQuery(id+"F0.wireOp",EDGE,"E23.filletArc"),sQuery(id+"F0.wireOp",EDGE,"E24.filletArc"),sQuery(id+"F0.wireOp",EDGE,"E25.filletArc"),sQuery(id+"F0.wireOp",EDGE,"E26.filletArc"),sQuery(id+"F0.wireOp",EDGE,"E27.filletArc"),sQuery(id+"F0.wireOp",EDGE,"E28.filletArc"),sQuery(id+"F0.wireOp",EDGE,"E29.filletArc")])],"isStart":false}),makeQuery(id+"F3.opExtrude","CAP_FACE",FACE,{"disambiguationData":[OSD([sQuery(id+"F2.wireOp",EDGE,"E30.bottom"),subQ0,sQuery(id+"F2.wireOp",EDGE,"E30.left"),sQuery(id+"F2.wireOp",EDGE,"E30.right")])],"isStart":false})]}),makeQuery(id+"F3.boolean.opBoolean","COPY",FACE,{"derivedFrom":makeQuery(id+"F3.opExtrude","SWEPT_FACE",FACE,{"disambiguationData":[OSD([subQ0])]})})],"blendedInto":[makeQuery(id+"F3.boolean.opBoolean","COPY",FACE,{"derivedFrom":makeQuery(id+"F3.opExtrude","SWEPT_FACE",FACE,{"disambiguationData":[OSD([subQ0])]})})]});}
            fillet(context, id + "F18", {"entities" : qUnion([Q0]), "radius" : 1.5 * mm, "tangentPropagation" : true, "allowEdgeOverflow" : false});
        }
    });
